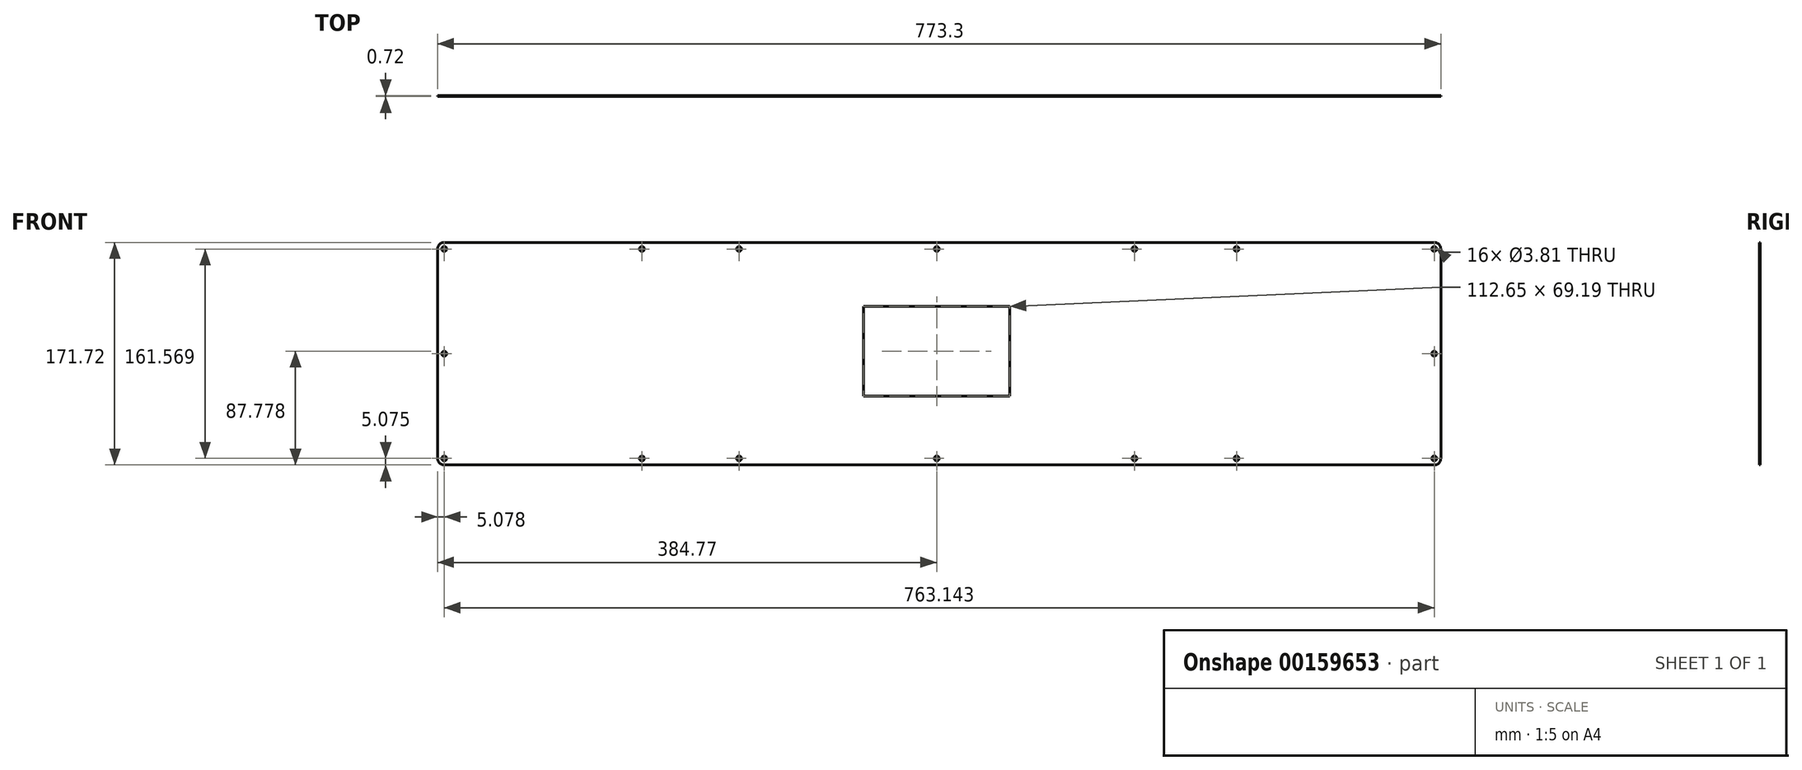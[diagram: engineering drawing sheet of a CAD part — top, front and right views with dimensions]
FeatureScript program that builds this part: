
annotation { "Feature Type Name" : "Feature", "Feature Type Description" : "" }
export const myFeature = defineFeature(function(context is Context, id is Id, definition is map)
    precondition{}
    {
        {
            var Q0;
            Q0=qCreatedBy(makeId("Front.planeOp"),FACE);
            var sketch = newSketch(context, id + "F0", { "sketchPlane" : qUnion([Q0])});
            skLineSegment(sketch, "E0.bottom", {"start": v(376.5, 75.7) * mm, "end": v(-376.5, 75.7) * mm});
            skLineSegment(sketch, "E0.top", {"start": v(376.5, -75.7) * mm, "end": v(-376.5, -75.7) * mm});
            skLineSegment(sketch, "E0.left", {"start": v(376.5, 75.7) * mm, "end": v(376.5, -75.7) * mm});
            skLineSegment(sketch, "E0.right", {"start": v(-376.5, 75.7) * mm, "end": v(-376.5, -75.7) * mm});
            skPoint(sketch, "E0.middle", {"position": v(0, 0) * mm});
            skLineSegment(sketch, "E1.bottom", {"start": v(54.44, 36.51) * mm, "end": v(-58.2, 36.51) * mm});
            skLineSegment(sketch, "E1.top", {"start": v(54.44, -32.68) * mm, "end": v(-58.2, -32.68) * mm});
            skLineSegment(sketch, "E1.left", {"start": v(54.44, 36.51) * mm, "end": v(54.44, -32.68) * mm});
            skLineSegment(sketch, "E1.right", {"start": v(-58.2, 36.51) * mm, "end": v(-58.2, -32.68) * mm});
            skSolve(sketch);
        }
        {
            var Q0;
            Q0 = qSketchRegion(id + "F0", true);
            extrude(context, id + "F1", {"entities" : qUnion([Q0]), "depth" : 0.72 * mm});
        }
        {
            var Q0;
            Q0=makeQuery(id+"F1.opExtrude","SWEPT_FACE",FACE,{"disambiguationData":[OSD([sQuery(id+"F0.wireOp",EDGE,"E0.bottom")])]});
            extrude(context, id + "F2", {"entities" : qUnion([Q0]), "operationType" : NewBodyOperationType.ADD, "depth" : 10.16 * mm});
        }
        {
            var Q0;
            Q0=makeQuery(id+"F1.opExtrude","SWEPT_FACE",FACE,{"disambiguationData":[OSD([sQuery(id+"F0.wireOp",EDGE,"E0.top")])]});
            extrude(context, id + "F3", {"entities" : qUnion([Q0]), "operationType" : NewBodyOperationType.ADD, "depth" : 10.16 * mm});
        }
        {
            var Q0;
            {var subQ0=sQuery(id+"F0.wireOp",EDGE,"E0.left");Q0=makeQuery(id+"F3.boolean.opBoolean","MERGE",FACE,{"derivedFrom":[makeQuery(id+"F2.boolean.opBoolean","MERGE",FACE,{"derivedFrom":[makeQuery(id+"F1.opExtrude","SWEPT_FACE",FACE,{"disambiguationData":[OSD([subQ0])]}),makeQuery(id+"F2.opExtrude","SWEPT_FACE",FACE,{"disambiguationData":[OSD([sQuery(id+"F0.wireOp",EDGE,"E0.bottom"),subQ0])]})]}),makeQuery(id+"F3.opExtrude","SWEPT_FACE",FACE,{"disambiguationData":[OSD([sQuery(id+"F0.wireOp",EDGE,"E0.top"),subQ0])]})]});}
            extrude(context, id + "F4", {"entities" : qUnion([Q0]), "operationType" : NewBodyOperationType.ADD, "depth" : 10.16 * mm});
        }
        {
            var Q0;
            {var subQ0=sQuery(id+"F0.wireOp",EDGE,"E0.right");Q0=makeQuery(id+"F3.boolean.opBoolean","MERGE",FACE,{"derivedFrom":[makeQuery(id+"F2.boolean.opBoolean","MERGE",FACE,{"derivedFrom":[makeQuery(id+"F1.opExtrude","SWEPT_FACE",FACE,{"disambiguationData":[OSD([subQ0])]}),makeQuery(id+"F2.opExtrude","SWEPT_FACE",FACE,{"disambiguationData":[OSD([sQuery(id+"F0.wireOp",EDGE,"E0.bottom"),subQ0])]})]}),makeQuery(id+"F3.opExtrude","SWEPT_FACE",FACE,{"disambiguationData":[OSD([sQuery(id+"F0.wireOp",EDGE,"E0.top"),subQ0])]})]});}
            extrude(context, id + "F5", {"entities" : qUnion([Q0]), "operationType" : NewBodyOperationType.ADD, "depth" : 10.16 * mm});
        }
        {
            var Q0;
            {var subQ0=sQuery(id+"F0.wireOp",EDGE,"E0.top");var subQ1=sQuery(id+"F0.wireOp",EDGE,"E0.bottom");Q0=makeQuery(id+"F3.boolean.opBoolean","MERGE",FACE,{"derivedFrom":[makeQuery(id+"F2.boolean.opBoolean","MERGE",FACE,{"derivedFrom":[makeQuery(id+"F1.opExtrude","CAP_FACE",FACE,{"disambiguationData":[OSD([subQ1,subQ0,sQuery(id+"F0.wireOp",EDGE,"E0.left"),sQuery(id+"F0.wireOp",EDGE,"E0.right"),sQuery(id+"F0.wireOp",EDGE,"E1.bottom"),sQuery(id+"F0.wireOp",EDGE,"E1.top"),sQuery(id+"F0.wireOp",EDGE,"E1.left"),sQuery(id+"F0.wireOp",EDGE,"E1.right")])],"isStart":true}),makeQuery(id+"F2.opExtrude","SWEPT_FACE",FACE,{"disambiguationData":[OSD([subQ1]),TDD([makeQuery(id+"F1.opExtrude","CAP_EDGE",EDGE,{"disambiguationData":[OSD([subQ1])],"isStart":true})])]})]}),makeQuery(id+"F3.opExtrude","SWEPT_FACE",FACE,{"disambiguationData":[OSD([subQ0]),TDD([makeQuery(id+"F1.opExtrude","CAP_EDGE",EDGE,{"disambiguationData":[OSD([subQ0])],"isStart":true})])]})]});}
            var sketch = newSketch(context, id + "F6", { "sketchPlane" : qUnion([Q0])});
            skCircle(sketch, "E2", {"center": v(-381.57, 80.78) * mm, "radius": 1.9 * mm});
            skCircle(sketch, "E3", {"center": v(1.88, 80.78) * mm, "radius": 1.9 * mm});
            skPoint(sketch, "E3.centerSnap0", {"position": v(1.88, 36.51) * mm});
            skCircle(sketch, "E4", {"center": v(381.57, 80.78) * mm, "radius": 1.9 * mm});
            skCircle(sketch, "E5.MirrorC", {"center": v(-381.57, -80.78) * mm, "radius": 1.9 * mm});
            skCircle(sketch, "E6.MirrorC", {"center": v(1.88, -80.78) * mm, "radius": 1.9 * mm});
            skCircle(sketch, "E7.MirrorC", {"center": v(381.57, -80.78) * mm, "radius": 1.9 * mm});
            skCircle(sketch, "E8", {"center": v(154.28, 80.78) * mm, "radius": 1.9 * mm});
            skCircle(sketch, "E9", {"center": v(229.17, 80.78) * mm, "radius": 1.9 * mm});
            skCircle(sketch, "E10", {"center": v(-150.52, 80.78) * mm, "radius": 1.9 * mm});
            skCircle(sketch, "E11", {"center": v(-229.17, 80.78) * mm, "radius": 1.9 * mm});
            skCircle(sketch, "E12", {"center": v(-381.57, 0) * mm, "radius": 1.9 * mm});
            skPoint(sketch, "E12.centerSnap0", {"position": v(-386.65, 0) * mm});
            skCircle(sketch, "E13", {"center": v(381.57, 0) * mm, "radius": 1.9 * mm});
            skPoint(sketch, "E13.centerSnap0", {"position": v(386.65, 0) * mm});
            skCircle(sketch, "E14.MirrorC", {"center": v(-229.17, -80.78) * mm, "radius": 1.9 * mm});
            skCircle(sketch, "E15.MirrorC", {"center": v(-150.52, -80.78) * mm, "radius": 1.9 * mm});
            skCircle(sketch, "E16.MirrorC", {"center": v(154.28, -80.78) * mm, "radius": 1.9 * mm});
            skCircle(sketch, "E17.MirrorC", {"center": v(229.17, -80.78) * mm, "radius": 1.9 * mm});
            skSolve(sketch);
        }
        {
            var Q0;
            Q0 = qSketchRegion(id + "F6", true);
            extrude(context, id + "F7", {"entities" : qUnion([Q0]), "operationType" : NewBodyOperationType.REMOVE, "endBound" : BoundingType.THROUGH_ALL, "oppositeDirection" : true, "depth" : 25.4 * mm});
        }
        {
            var Q0;
            Q0=makeQuery(id+"F4.opExtrude","CAP_EDGE",EDGE,{"disambiguationData":[OSD([sQuery(id+"F0.wireOp",EDGE,"E0.bottom"),sQuery(id+"F0.wireOp",EDGE,"E0.left")])],"isStart":false});
            var Q1;
            Q1=makeQuery(id+"F4.opExtrude","CAP_EDGE",EDGE,{"disambiguationData":[OSD([sQuery(id+"F0.wireOp",EDGE,"E0.top"),sQuery(id+"F0.wireOp",EDGE,"E0.left")])],"isStart":false});
            var Q2;
            Q2=makeQuery(id+"F5.opExtrude","CAP_EDGE",EDGE,{"disambiguationData":[OSD([sQuery(id+"F0.wireOp",EDGE,"E0.top"),sQuery(id+"F0.wireOp",EDGE,"E0.right")])],"isStart":false});
            var Q3;
            Q3=makeQuery(id+"F5.opExtrude","CAP_EDGE",EDGE,{"disambiguationData":[OSD([sQuery(id+"F0.wireOp",EDGE,"E0.bottom"),sQuery(id+"F0.wireOp",EDGE,"E0.right")])],"isStart":false});
            fillet(context, id + "F8", {"entities" : qUnion([Q0, Q1, Q2, Q3]), "radius" : 5.08 * mm, "tangentPropagation" : true, "allowEdgeOverflow" : false});
        }
    });
